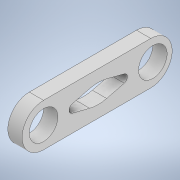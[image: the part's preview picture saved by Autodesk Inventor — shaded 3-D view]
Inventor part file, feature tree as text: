
AUTODESK INVENTOR PART (.ipt)
format: ipt  version: 2022 (Build 260153000, 153)  size: 124,928 bytes
history: native  units: mm
features: extrude x1, sketch x1
ambient origin geometry x8: Origin, YZ Plane, XZ Plane, XY Plane, X Axis, Y Axis, Z Axis, Center Point
bodies: Solid1 (feature_tree)
feature tree (2):
  extrude  "Extrusion1"  Depth=2.0mm
  sketch  "Sketch1"  dims[d0=6.0mm d1=15.0mm d2=4.0mm d3=2.0mm d4=0.0mm]
